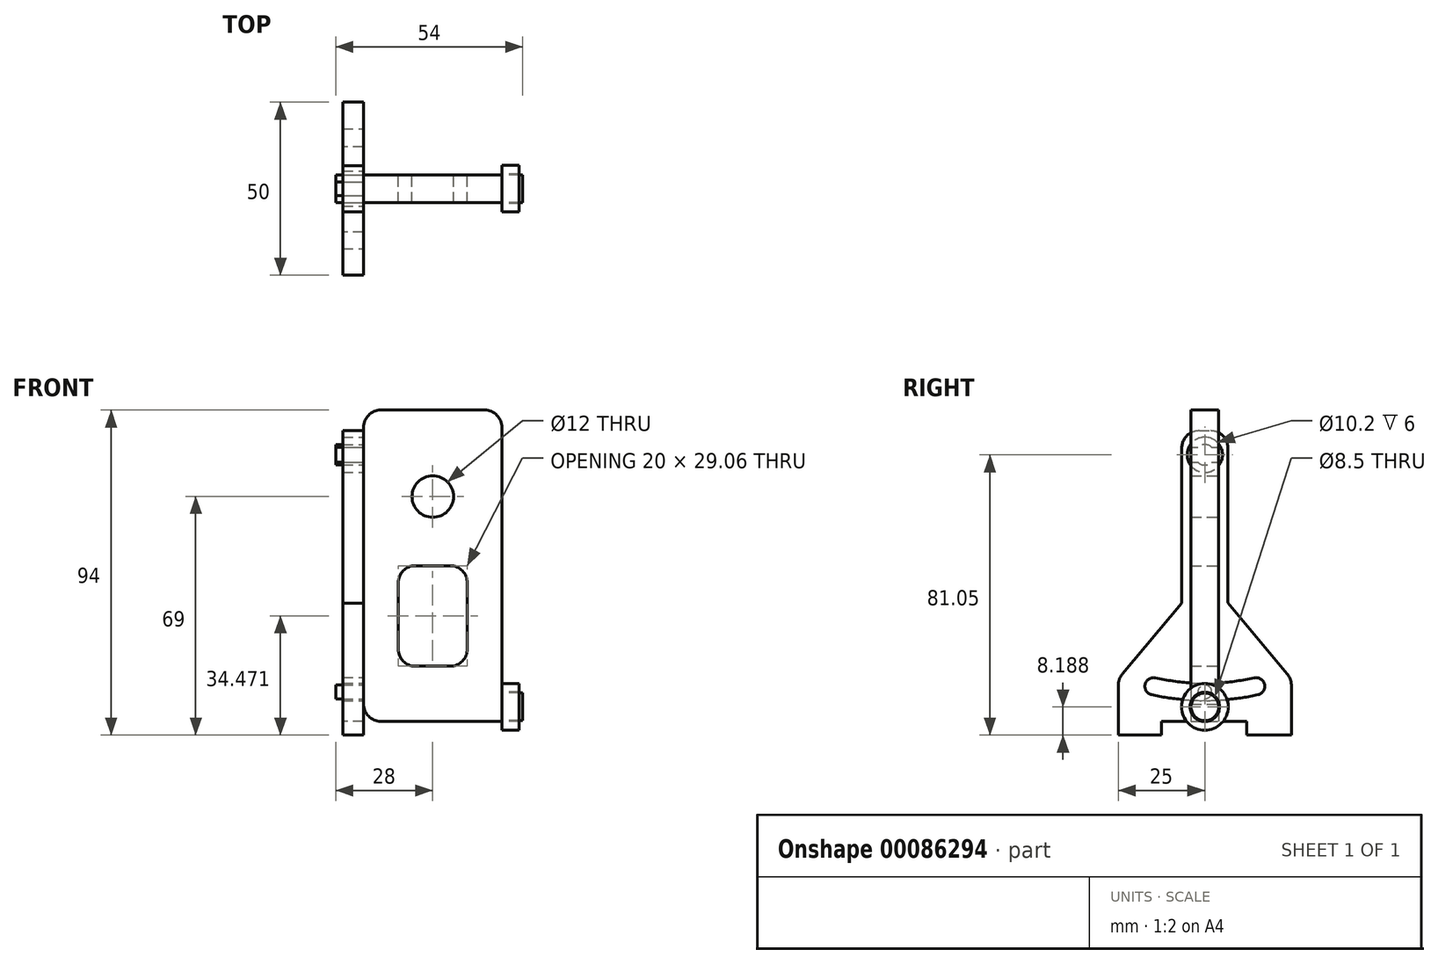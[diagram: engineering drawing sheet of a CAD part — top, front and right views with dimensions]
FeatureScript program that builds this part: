
annotation { "Feature Type Name" : "Feature", "Feature Type Description" : "" }
export const myFeature = defineFeature(function(context is Context, id is Id, definition is map)
    precondition{}
    {
        {
            var Q0;
            Q0=qCreatedBy(makeId("Front.planeOp"),FACE);
            var sketch = newSketch(context, id + "F0", { "sketchPlane" : qUnion([Q0])});
            skLineSegment(sketch, "E0.bottom", {"start": v(20, 45) * mm, "end": v(-20, 45) * mm});
            skLineSegment(sketch, "E0.top", {"start": v(20, -45) * mm, "end": v(-20, -45) * mm});
            skLineSegment(sketch, "E0.left", {"start": v(20, 45) * mm, "end": v(20, -45) * mm});
            skLineSegment(sketch, "E0.right", {"start": v(-20, 45) * mm, "end": v(-20, -45) * mm});
            skPoint(sketch, "E0.middle", {"position": v(0, 0) * mm});
            skLineSegment(sketch, "E1", {"start": v(0, 11.25) * mm, "end": v(0, 0) * mm, "construction": true});
            skPoint(sketch, "E2.orphan", {"position": v(0, -45) * mm});
            skLineSegment(sketch, "E3", {"start": v(0, 20) * mm, "end": v(-20, 20) * mm, "construction": true});
            skPoint(sketch, "E4.middle", {"position": v(-20, 20) * mm});
            skLineSegment(sketch, "E5", {"start": v(0, 0) * mm, "end": v(0, -45) * mm, "construction": true});
            skLineSegment(sketch, "E6.bottom", {"start": v(10, -45) * mm, "end": v(-10, -45) * mm});
            skLineSegment(sketch, "E6.top", {"start": v(10, 0) * mm, "end": v(-10, 0) * mm});
            skLineSegment(sketch, "E6.right", {"start": v(-10, -29.06) * mm, "end": v(-10, 0) * mm});
            skPoint(sketch, "E6.middle", {"position": v(0, -22.5) * mm});
            skLineSegment(sketch, "E7", {"start": v(-10, -29.06) * mm, "end": v(10, -29.06) * mm});
            skLineSegment(sketch, "E8", {"start": v(10, -29.06) * mm, "end": v(10, 0) * mm});
            skCircle(sketch, "E9", {"center": v(0, 20) * mm, "radius": 6 * mm});
            skSolve(sketch);
        }
        {
            var Q0;
            {var subQ0=sQuery(id+"F0.wireOp",EDGE,"E0.bottom");Q0=makeQuery(id+"F0.imprint","IMPRINT",FACE,{"disambiguationData":[TD([[makeQuery(id+"F0.imprint","IMPRINT",EDGE,{"derivedFrom":subQ0}),1.0]])]});}
            extrude(context, id + "F1", {"entities" : qUnion([Q0]), "depth" : 4 * mm});
        }
        {
            var Q0;
            Q0=makeQuery(id+"F1.opExtrude","SWEPT_FACE",FACE,{"disambiguationData":[OSD([sQuery(id+"F0.wireOp",EDGE,"E0.right")])]});
            var sketch = newSketch(context, id + "F2", { "sketchPlane" : qUnion([Q0])});
            skLineSegment(sketch, "E10", {"start": v(0, 32.05) * mm, "end": v(2, 32.05) * mm, "construction": true});
            skCircle(sketch, "E11", {"center": v(2, 32.05) * mm, "radius": 5.1 * mm});
            skPoint(sketch, "E12.orphan", {"position": v(2, 45) * mm});
            skLineSegment(sketch, "E13.trimOffspring", {"start": v(4, 32.05) * mm, "end": v(7.1, 32.05) * mm, "construction": true});
            skCircle(sketch, "E14", {"center": v(2, 32.05) * mm, "radius": 2.95 * mm});
            skLineSegment(sketch, "E15.bottom", {"start": v(8.67, 39) * mm, "end": v(-4.67, 39) * mm});
            skLineSegment(sketch, "E15.right", {"start": v(-4.67, 39) * mm, "end": v(-4.67, -10.68) * mm});
            skPoint(sketch, "E15.middle", {"position": v(2, 0) * mm});
            skPoint(sketch, "E15.middle.positionSnap0", {"position": v(0, 0) * mm});
            skPoint(sketch, "E15.centerSnap0", {"position": v(0, 0) * mm});
            skLineSegment(sketch, "E16.bottom", {"start": v(27, -45) * mm, "end": v(-23, -45) * mm});
            skLineSegment(sketch, "E16.left", {"start": v(27, -45) * mm, "end": v(27, -32.73) * mm});
            skLineSegment(sketch, "E16.right", {"start": v(-23, -45) * mm, "end": v(-23, -32.73) * mm});
            skPoint(sketch, "E16.middle", {"position": v(2, -32.73) * mm});
            skPoint(sketch, "E16.middle.positionSnap0", {"position": v(2, -39) * mm});
            skPoint(sketch, "E16.centerSnap0", {"position": v(2, -39) * mm});
            skPoint(sketch, "E17.orphan", {"position": v(-4.67, -39) * mm});
            skPoint(sketch, "E18.orphan", {"position": v(8.67, -39) * mm});
            skLineSegment(sketch, "E19", {"start": v(8.67, 39) * mm, "end": v(8.67, -10.83) * mm});
            skPoint(sketch, "E20.orphan", {"position": v(-23, -20.46) * mm});
            skPoint(sketch, "E21.orphan", {"position": v(27, -20.46) * mm});
            skArc(sketch, "E22", {"start": v(-13.38, -37.32) * mm, "mid": v(2, -39) * mm, "end": v(17.38, -37.32) * mm});
            skArc(sketch, "E23", {"start": v(-12.3, -32.43) * mm, "mid": v(2, -34) * mm, "end": v(16.3, -32.43) * mm});
            skLineSegment(sketch, "E24", {"start": v(2, 32.05) * mm, "end": v(-12.84, -34.88) * mm, "construction": true});
            skLineSegment(sketch, "E25", {"start": v(2, 32.05) * mm, "end": v(17.38, -37.32) * mm, "construction": true});
            skLineSegment(sketch, "E26", {"start": v(2, -39) * mm, "end": v(2, 32.05) * mm, "construction": true});
            skArc(sketch, "E27", {"start": v(-12.3, -32.43) * mm, "mid": v(-15.28, -34.33) * mm, "end": v(-13.38, -37.32) * mm});
            skArc(sketch, "E28", {"start": v(17.38, -37.32) * mm, "mid": v(19.28, -34.33) * mm, "end": v(16.3, -32.43) * mm});
            skCircle(sketch, "E29", {"center": v(2, -36.5) * mm, "radius": 2 * mm});
            skPoint(sketch, "E30.trimOffspring.end.orphan", {"position": v(2, -34) * mm});
            skLineSegment(sketch, "E31.1.0", {"start": v(2, 32.05) * mm, "end": v(2, -36.5) * mm, "construction": true});
            skLineSegment(sketch, "E31.2.0", {"start": v(2, 32.05) * mm, "end": v(16.84, -34.88) * mm, "construction": true});
            skLineSegment(sketch, "E31.anchor2", {"start": v(2, 32.05) * mm, "end": v(16.84, -34.88) * mm, "construction": true});
            skLineSegment(sketch, "E32", {"start": v(-23, -32.73) * mm, "end": v(-4.67, -10.68) * mm});
            skLineSegment(sketch, "E33", {"start": v(8.67, -10.83) * mm, "end": v(27, -32.73) * mm});
            skSolve(sketch);
        }
        {
            var Q0;
            Q0=makeQuery(id+"F2.imprint","IMPRINT",FACE,{"disambiguationData":[TD([[makeQuery(id+"F2.imprint","IMPRINT",EDGE,{"derivedFrom":sQuery(id+"F2.wireOp",EDGE,"E14")}),1.0]])]});
            var Q1;
            {var subQ0=sQuery(id+"F2.wireOp",EDGE,"E14");var subQ1=makeQuery(id+"F1.opExtrude","CAP_EDGE",EDGE,{"disambiguationData":[OSD([sQuery(id+"F0.wireOp",EDGE,"E0.right")])],"isStart":false});var subQ2=makeQuery(id+"F2.imprint","INTERSECT",VERTEX,{"disambiguationData":[OD(0.0)],"derivedFrom":[subQ1,subQ0]});Q1=makeQuery(id+"F2.imprint","IMPRINT",FACE,{"disambiguationData":[TD([[makeQuery(id+"F2.imprint","IMPRINT",EDGE,{"disambiguationData":[TD([[subQ2,1.0]])],"derivedFrom":subQ0}),1.0]])]});}
            var Q2;
            {var subQ0=sQuery(id+"F2.wireOp",EDGE,"E14");var subQ1=makeQuery(id+"F1.opExtrude","CAP_EDGE",EDGE,{"disambiguationData":[OSD([sQuery(id+"F0.wireOp",EDGE,"E0.right")])],"isStart":true});var subQ2=makeQuery(id+"F2.imprint","INTERSECT",VERTEX,{"disambiguationData":[OD(0.0)],"derivedFrom":[subQ1,subQ0]});Q2=makeQuery(id+"F2.imprint","IMPRINT",FACE,{"disambiguationData":[TD([[makeQuery(id+"F2.imprint","IMPRINT",EDGE,{"disambiguationData":[TD([[subQ2,-1.0]])],"derivedFrom":subQ0}),1.0]])]});}
            extrude(context, id + "F3", {"entities" : qUnion([Q0, Q1, Q2]), "operationType" : NewBodyOperationType.ADD, "depth" : 8 * mm});
        }
        {
            var Q0;
            {var subQ1=sQuery(id+"F2.wireOp",EDGE,"E15.right");Q0=makeQuery(id+"F2.imprint","IMPRINT",FACE,{"disambiguationData":[TD([[makeQuery(id+"F2.imprint","IMPRINT",EDGE,{"derivedFrom":subQ1}),1.0]])]});}
            var Q1;
            {var subQ3=sQuery(id+"F2.wireOp",EDGE,"E16.left");Q1=makeQuery(id+"F2.imprint","IMPRINT",FACE,{"disambiguationData":[TD([[makeQuery(id+"F2.imprint","IMPRINT",EDGE,{"derivedFrom":subQ3}),1.0]])]});}
            var Q2;
            {var subQ0=sQuery(id+"F2.wireOp",EDGE,"E16.bottom");var subQ1=sQuery(id+"F0.wireOp",EDGE,"E0.right");var subQ2=makeQuery(id+"F1.opExtrude","CAP_EDGE",EDGE,{"disambiguationData":[OSD([subQ1])],"isStart":true});var subQ3=makeQuery(id+"F2.imprint","INTERSECT",VERTEX,{"derivedFrom":[subQ2,subQ0]});Q2=makeQuery(id+"F2.imprint","IMPRINT",FACE,{"disambiguationData":[TD([[makeQuery(id+"F2.imprint","IMPRINT",EDGE,{"disambiguationData":[TD([[subQ3,1.0]])],"derivedFrom":subQ0}),-1.0]])]});}
            var Q3;
            Q3=makeQuery(id+"F2.imprint","IMPRINT",FACE,{"disambiguationData":[TD([[makeQuery(id+"F2.imprint","IMPRINT",EDGE,{"derivedFrom":sQuery(id+"F2.wireOp",EDGE,"E14")}),-1.0]])]});
            var Q4;
            {var subQ0=sQuery(id+"F2.wireOp",EDGE,"E11");var subQ1=sQuery(id+"F0.wireOp",EDGE,"E0.right");var subQ2=makeQuery(id+"F1.opExtrude","CAP_EDGE",EDGE,{"disambiguationData":[OSD([subQ1])],"isStart":false});var subQ3=makeQuery(id+"F2.imprint","INTERSECT",VERTEX,{"derivedFrom":[subQ2,subQ0]});Q4=makeQuery(id+"F2.imprint","IMPRINT",FACE,{"disambiguationData":[TD([[makeQuery(id+"F2.imprint","IMPRINT",EDGE,{"disambiguationData":[TD([[subQ3,1.0]])],"derivedFrom":subQ0}),-1.0]])]});}
            var Q5;
            {var subQ0=sQuery(id+"F2.wireOp",EDGE,"E11");var subQ1=sQuery(id+"F0.wireOp",EDGE,"E0.right");var subQ2=makeQuery(id+"F1.opExtrude","CAP_EDGE",EDGE,{"disambiguationData":[OSD([subQ1])],"isStart":false});var subQ3=makeQuery(id+"F2.imprint","INTERSECT",VERTEX,{"derivedFrom":[subQ2,subQ0]});Q5=makeQuery(id+"F2.imprint","IMPRINT",FACE,{"disambiguationData":[TD([[makeQuery(id+"F2.imprint","IMPRINT",EDGE,{"disambiguationData":[TD([[subQ3,-1.0]])],"derivedFrom":subQ0}),-1.0]])]});}
            extrude(context, id + "F4", {"entities" : qUnion([Q0, Q1, Q2, Q3, Q4, Q5]), "depth" : 6 * mm});
        }
        {
            var Q0;
            {var subQ0=sQuery(id+"F2.wireOp",EDGE,"E29");var subQ1=sQuery(id+"F0.wireOp",EDGE,"E0.right");var subQ2=makeQuery(id+"F2.imprint","INTERSECT",VERTEX,{"derivedFrom":[makeQuery(id+"F1.opExtrude","CAP_EDGE",EDGE,{"disambiguationData":[OSD([subQ1])],"isStart":true}),subQ0]});Q0=makeQuery(id+"F2.imprint","IMPRINT",FACE,{"disambiguationData":[TD([[makeQuery(id+"F2.imprint","IMPRINT",EDGE,{"disambiguationData":[TD([[subQ2,1.0]])],"derivedFrom":subQ0}),1.0]])]});}
            extrude(context, id + "F5", {"entities" : qUnion([Q0]), "operationType" : NewBodyOperationType.ADD, "depth" : 8 * mm});
        }
        {
            var Q0;
            Q0=makeQuery(id+"F4.opExtrude","SWEPT_FACE",FACE,{"disambiguationData":[OSD([sQuery(id+"F2.wireOp",EDGE,"E16.bottom")])]});
            var sketch = newSketch(context, id + "F6", { "sketchPlane" : qUnion([Q0])});
            skLineSegment(sketch, "E34", {"start": v(-20, -10.08) * mm, "end": v(-26, -10.08) * mm});
            skLineSegment(sketch, "E35", {"start": v(-20, 14.57) * mm, "end": v(-26, 14.57) * mm});
            skSolve(sketch);
        }
        {
            var Q0;
            {var subQ0=sQuery(id+"F6.wireOp",EDGE,"E34");Q0=makeQuery(id+"F6.imprint","IMPRINT",FACE,{"disambiguationData":[TD([[makeQuery(id+"F6.imprint","IMPRINT",EDGE,{"derivedFrom":subQ0}),1.0]])]});}
            var Q1;
            {var subQ0=sQuery(id+"F6.wireOp",EDGE,"E35");Q1=makeQuery(id+"F6.imprint","IMPRINT",FACE,{"disambiguationData":[TD([[makeQuery(id+"F6.imprint","IMPRINT",EDGE,{"derivedFrom":subQ0}),-1.0]])]});}
            extrude(context, id + "F7", {"entities" : qUnion([Q0, Q1]), "operationType" : NewBodyOperationType.ADD, "depth" : 4 * mm});
        }
        {
            var Q0;
            Q0=makeQuery(id+"F1.opExtrude","SWEPT_EDGE",EDGE,{"disambiguationData":[OSD([sQuery(id+"F0.wireOp",EDGE,"E0.top"),sQuery(id+"F0.wireOp",EDGE,"E0.right")])]});
            var Q1;
            Q1=makeQuery(id+"F1.opExtrude","SWEPT_EDGE",EDGE,{"disambiguationData":[OSD([sQuery(id+"F0.wireOp",EDGE,"E6.top"),sQuery(id+"F0.wireOp",EDGE,"E6.right")])]});
            var Q2;
            Q2=makeQuery(id+"F1.opExtrude","SWEPT_EDGE",EDGE,{"disambiguationData":[OSD([sQuery(id+"F0.wireOp",EDGE,"E6.right"),sQuery(id+"F0.wireOp",EDGE,"E7")])]});
            var Q3;
            Q3=makeQuery(id+"F1.opExtrude","SWEPT_EDGE",EDGE,{"disambiguationData":[OSD([sQuery(id+"F0.wireOp",EDGE,"E0.top"),sQuery(id+"F0.wireOp",EDGE,"E0.right")])]});
            var Q4;
            Q4=makeQuery(id+"F1.opExtrude","SWEPT_EDGE",EDGE,{"disambiguationData":[OSD([sQuery(id+"F0.wireOp",EDGE,"E6.top"),sQuery(id+"F0.wireOp",EDGE,"E6.right")])]});
            var Q5;
            Q5=makeQuery(id+"F1.opExtrude","SWEPT_EDGE",EDGE,{"disambiguationData":[OSD([sQuery(id+"F0.wireOp",EDGE,"E6.top"),sQuery(id+"F0.wireOp",EDGE,"E8")])]});
            var Q6;
            Q6=makeQuery(id+"F1.opExtrude","SWEPT_EDGE",EDGE,{"disambiguationData":[OSD([sQuery(id+"F0.wireOp",EDGE,"E6.top"),sQuery(id+"F0.wireOp",EDGE,"E6.right")])]});
            var Q7;
            Q7=makeQuery(id+"F1.opExtrude","SWEPT_EDGE",EDGE,{"disambiguationData":[OSD([sQuery(id+"F0.wireOp",EDGE,"E0.top"),sQuery(id+"F0.wireOp",EDGE,"E0.right")])]});
            var Q8;
            Q8=makeQuery(id+"F1.opExtrude","SWEPT_EDGE",EDGE,{"disambiguationData":[OSD([sQuery(id+"F0.wireOp",EDGE,"E6.top"),sQuery(id+"F0.wireOp",EDGE,"E6.right")])]});
            var Q9;
            Q9=makeQuery(id+"F1.opExtrude","SWEPT_EDGE",EDGE,{"disambiguationData":[OSD([sQuery(id+"F0.wireOp",EDGE,"E6.right"),sQuery(id+"F0.wireOp",EDGE,"E7")])]});
            var Q10;
            Q10=makeQuery(id+"F1.opExtrude","SWEPT_EDGE",EDGE,{"disambiguationData":[OSD([sQuery(id+"F0.wireOp",EDGE,"E0.bottom"),sQuery(id+"F0.wireOp",EDGE,"E0.left")])]});
            var Q11;
            Q11=makeQuery(id+"F1.opExtrude","SWEPT_EDGE",EDGE,{"disambiguationData":[OSD([sQuery(id+"F0.wireOp",EDGE,"E0.bottom"),sQuery(id+"F0.wireOp",EDGE,"E0.right")])]});
            var Q12;
            Q12=makeQuery(id+"F1.opExtrude","SWEPT_EDGE",EDGE,{"disambiguationData":[OSD([sQuery(id+"F0.wireOp",EDGE,"E7"),sQuery(id+"F0.wireOp",EDGE,"E8")])]});
            fillet(context, id + "F8", {"entities" : qUnion([Q0, Q1, Q2, Q3, Q4, Q5, Q6, Q7, Q8, Q9, Q10, Q11, Q12]), "radius" : 5 * mm, "tangentPropagation" : true, "allowEdgeOverflow" : false});
        }
        {
            var Q0;
            Q0=makeQuery(id+"F2.imprint","IMPRINT",FACE,{"disambiguationData":[TD([[makeQuery(id+"F2.imprint","IMPRINT",EDGE,{"derivedFrom":sQuery(id+"F2.wireOp",EDGE,"E14")}),-1.0]])]});
            var Q1;
            {var subQ0=sQuery(id+"F2.wireOp",EDGE,"E16.bottom");var subQ1=makeQuery(id+"F4.opExtrude","CAP_EDGE",EDGE,{"disambiguationData":[OSD([subQ0])],"isStart":false});var subQ2=sQuery(id+"F2.wireOp",EDGE,"E16.right");var subQ3=sQuery(id+"F2.wireOp",EDGE,"E16.left");Q1=makeQuery(id+"F7.boolean.opBoolean","MERGE",FACE,{"derivedFrom":[makeQuery(id+"F4.opExtrude","CAP_FACE",FACE,{"disambiguationData":[OSD([sQuery(id+"F2.wireOp",EDGE,"E14"),sQuery(id+"F2.wireOp",EDGE,"E15.bottom"),sQuery(id+"F2.wireOp",EDGE,"E15.right"),subQ0,subQ3,subQ2,sQuery(id+"F2.wireOp",EDGE,"E19"),sQuery(id+"F2.wireOp",EDGE,"JuFRv1vB-4vIU-9MfZ-qExC-JWJJg4Ribfju"),sQuery(id+"F2.wireOp",EDGE,"cK3vs3qy-dBAu-Qh5l-vrAd-VUhtukTePDKx"),sQuery(id+"F2.wireOp",EDGE,"E22"),sQuery(id+"F2.wireOp",EDGE,"E23"),sQuery(id+"F2.wireOp",EDGE,"E27"),sQuery(id+"F2.wireOp",EDGE,"E28")])],"isStart":false}),makeQuery(id+"F7.opExtrude","SWEPT_FACE",FACE,{"disambiguationData":[OSD([subQ0]),TDD([makeQuery(id+"F6.imprint","IMPRINT",EDGE,{"disambiguationData":[TD([[makeQuery(id+"F6.imprint","INTERSECT",VERTEX,{"derivedFrom":[subQ1,sQuery(id+"F6.wireOp",EDGE,"E35")]}),1.0]])],"derivedFrom":subQ1})])]}),makeQuery(id+"F7.opExtrude","SWEPT_FACE",FACE,{"disambiguationData":[OSD([subQ0]),TDD([makeQuery(id+"F6.imprint","IMPRINT",EDGE,{"disambiguationData":[TD([[makeQuery(id+"F6.imprint","INTERSECT",VERTEX,{"derivedFrom":[subQ1,sQuery(id+"F6.wireOp",EDGE,"E34")]}),-1.0]])],"derivedFrom":subQ1})])]})]});}
            extrude(context, id + "F9", {"entities" : qUnion([Q0]), "operationType" : NewBodyOperationType.REMOVE, "endBound" : BoundingType.UP_TO_SURFACE, "endBoundEntityFace" : qUnion([Q1]), "depth" : 25 * mm});
        }
        {
            var Q0;
            Q0=makeQuery(id+"F4.opExtrude","SWEPT_EDGE",EDGE,{"disambiguationData":[OSD([sQuery(id+"F2.wireOp",EDGE,"E16.right"),sQuery(id+"F2.wireOp",EDGE,"cK3vs3qy-dBAu-Qh5l-vrAd-VUhtukTePDKx")])]});
            var Q1;
            Q1=makeQuery(id+"F4.opExtrude","SWEPT_EDGE",EDGE,{"disambiguationData":[OSD([sQuery(id+"F2.wireOp",EDGE,"E16.left"),sQuery(id+"F2.wireOp",EDGE,"JuFRv1vB-4vIU-9MfZ-qExC-JWJJg4Ribfju")])]});
            var Q2;
            Q2=makeQuery(id+"F4.opExtrude","SWEPT_EDGE",EDGE,{"disambiguationData":[OSD([sQuery(id+"F2.wireOp",EDGE,"E15.bottom"),sQuery(id+"F2.wireOp",EDGE,"E15.right")])]});
            var Q3;
            Q3=makeQuery(id+"F4.opExtrude","SWEPT_EDGE",EDGE,{"disambiguationData":[OSD([sQuery(id+"F2.wireOp",EDGE,"E15.bottom"),sQuery(id+"F2.wireOp",EDGE,"E19")])]});
            var Q4;
            Q4=makeQuery(id+"F7.opExtrude","CAP_EDGE",EDGE,{"disambiguationData":[OSD([sQuery(id+"F6.wireOp",EDGE,"E34")])],"isStart":true});
            var Q5;
            Q5=makeQuery(id+"F7.opExtrude","CAP_EDGE",EDGE,{"disambiguationData":[OSD([sQuery(id+"F6.wireOp",EDGE,"E35")])],"isStart":true});
            fillet(context, id + "F10", {"entities" : qUnion([Q0, Q1, Q2, Q3, Q4, Q5]), "radius" : 5 * mm, "tangentPropagation" : true, "allowEdgeOverflow" : false});
        }
        {
            var Q0;
            Q0=makeQuery(id+"F1.opExtrude","CAP_FACE",FACE,{"disambiguationData":[OSD([sQuery(id+"F0.wireOp",EDGE,"E0.bottom"),sQuery(id+"F0.wireOp",EDGE,"E0.top"),sQuery(id+"F0.wireOp",EDGE,"E0.left"),sQuery(id+"F0.wireOp",EDGE,"E0.right"),sQuery(id+"F0.wireOp",EDGE,"E6.top"),sQuery(id+"F0.wireOp",EDGE,"E6.left"),sQuery(id+"F0.wireOp",EDGE,"E6.right"),sQuery(id+"F0.wireOp",EDGE,"b41583f6-e2e4-40b4-8a0d-62e36b116213.0"),sQuery(id+"F0.wireOp",EDGE,"b41583f6-e2e4-40b4-8a0d-62e36b116213.1"),sQuery(id+"F0.wireOp",EDGE,"b41583f6-e2e4-40b4-8a0d-62e36b116213.2"),sQuery(id+"F0.wireOp",EDGE,"b41583f6-e2e4-40b4-8a0d-62e36b116213.3"),sQuery(id+"F0.wireOp",EDGE,"b41583f6-e2e4-40b4-8a0d-62e36b116213.4"),sQuery(id+"F0.wireOp",EDGE,"b41583f6-e2e4-40b4-8a0d-62e36b116213.5")])],"isStart":false});
            extrude(context, id + "F11", {"entities" : qUnion([Q0]), "operationType" : NewBodyOperationType.ADD, "depth" : 2 * mm, "hasSecondDirection" : true, "secondDirectionOppositeDirection" : true, "secondDirectionDepth" : 6 * mm});
        }
        {
            var Q0;
            {var subQ0=sQuery(id+"F0.wireOp",EDGE,"E0.left");Q0=makeQuery(id+"F11.boolean.opBoolean","MERGE",FACE,{"derivedFrom":[makeQuery(id+"F1.opExtrude","SWEPT_FACE",FACE,{"disambiguationData":[OSD([subQ0])]}),makeQuery(id+"F11.opExtrude","SWEPT_FACE",FACE,{"disambiguationData":[OSD([subQ0])]})]});}
            var sketch = newSketch(context, id + "F12", { "sketchPlane" : qUnion([Q0])});
            skCircle(sketch, "E36", {"center": v(-2, -40.81) * mm, "radius": 4 * mm});
            skPoint(sketch, "E36.centerSnap0", {"position": v(-2, -45) * mm});
            skCircle(sketch, "E37", {"center": v(-2, -40.81) * mm, "radius": 6.75 * mm});
            skCircle(sketch, "E38", {"center": v(-2, -40.81) * mm, "radius": 4.25 * mm});
            skSolve(sketch);
        }
        {
            var Q0;
            {var subQ0=sQuery(id+"F12.wireOp",EDGE,"E36");var subQ1=sQuery(id+"F0.wireOp",EDGE,"E0.left");var subQ2=makeQuery(id+"F12.imprint","INTERSECT",VERTEX,{"derivedFrom":[makeQuery(id+"F11.opExtrude","CAP_EDGE",EDGE,{"disambiguationData":[OSD([subQ1])],"isStart":true}),subQ0]});Q0=makeQuery(id+"F12.imprint","IMPRINT",FACE,{"disambiguationData":[TD([[makeQuery(id+"F12.imprint","IMPRINT",EDGE,{"disambiguationData":[TD([[subQ2,-1.0]])],"derivedFrom":subQ0}),1.0]])]});}
            extrude(context, id + "F13", {"entities" : qUnion([Q0]), "operationType" : NewBodyOperationType.ADD, "depth" : 6 * mm});
        }
        {
            var Q0;
            {var subQ0=sQuery(id+"F0.wireOp",EDGE,"E0.left");var subQ1=sQuery(id+"F0.wireOp",EDGE,"E0.top");var subQ2=makeQuery(id+"F11.boolean.opBoolean","MERGE",EDGE,{"derivedFrom":[makeQuery(id+"F1.opExtrude","SWEPT_EDGE",EDGE,{"disambiguationData":[OSD([subQ1,subQ0])]}),makeQuery(id+"F11.opExtrude","SWEPT_EDGE",EDGE,{"disambiguationData":[OSD([subQ1,subQ0])]})]});Q0=makeQuery(id+"F12.imprint","IMPRINT",FACE,{"disambiguationData":[TD([[makeQuery(id+"F12.imprint","IMPRINT",EDGE,{"derivedFrom":subQ2}),-1.0]])]});}
            var Q1;
            {var subQ1=sQuery(id+"F0.wireOp",EDGE,"E0.left");var subQ6=sQuery(id+"F0.wireOp",EDGE,"E0.top");var subQ7=makeQuery(id+"F11.boolean.opBoolean","MERGE",EDGE,{"derivedFrom":[makeQuery(id+"F1.opExtrude","SWEPT_EDGE",EDGE,{"disambiguationData":[OSD([subQ6,subQ1])]}),makeQuery(id+"F11.opExtrude","SWEPT_EDGE",EDGE,{"disambiguationData":[OSD([subQ6,subQ1])]})]});Q1=makeQuery(id+"F12.imprint","IMPRINT",FACE,{"disambiguationData":[TD([[makeQuery(id+"F12.imprint","IMPRINT",EDGE,{"derivedFrom":subQ7}),1.0]])]});}
            var Q2;
            {var subQ0=sQuery(id+"F12.wireOp",EDGE,"E37");var subQ1=sQuery(id+"F0.wireOp",EDGE,"E0.left");var subQ2=makeQuery(id+"F11.opExtrude","CAP_EDGE",EDGE,{"disambiguationData":[OSD([subQ1])],"isStart":true});var subQ3=makeQuery(id+"F12.imprint","INTERSECT",VERTEX,{"derivedFrom":[subQ2,subQ0]});Q2=makeQuery(id+"F12.imprint","IMPRINT",FACE,{"disambiguationData":[TD([[makeQuery(id+"F12.imprint","IMPRINT",EDGE,{"disambiguationData":[TD([[subQ3,-1.0]])],"derivedFrom":subQ0}),1.0]])]});}
            extrude(context, id + "F14", {"entities" : qUnion([Q0, Q1, Q2]), "depth" : 5 * mm});
        }
    });
